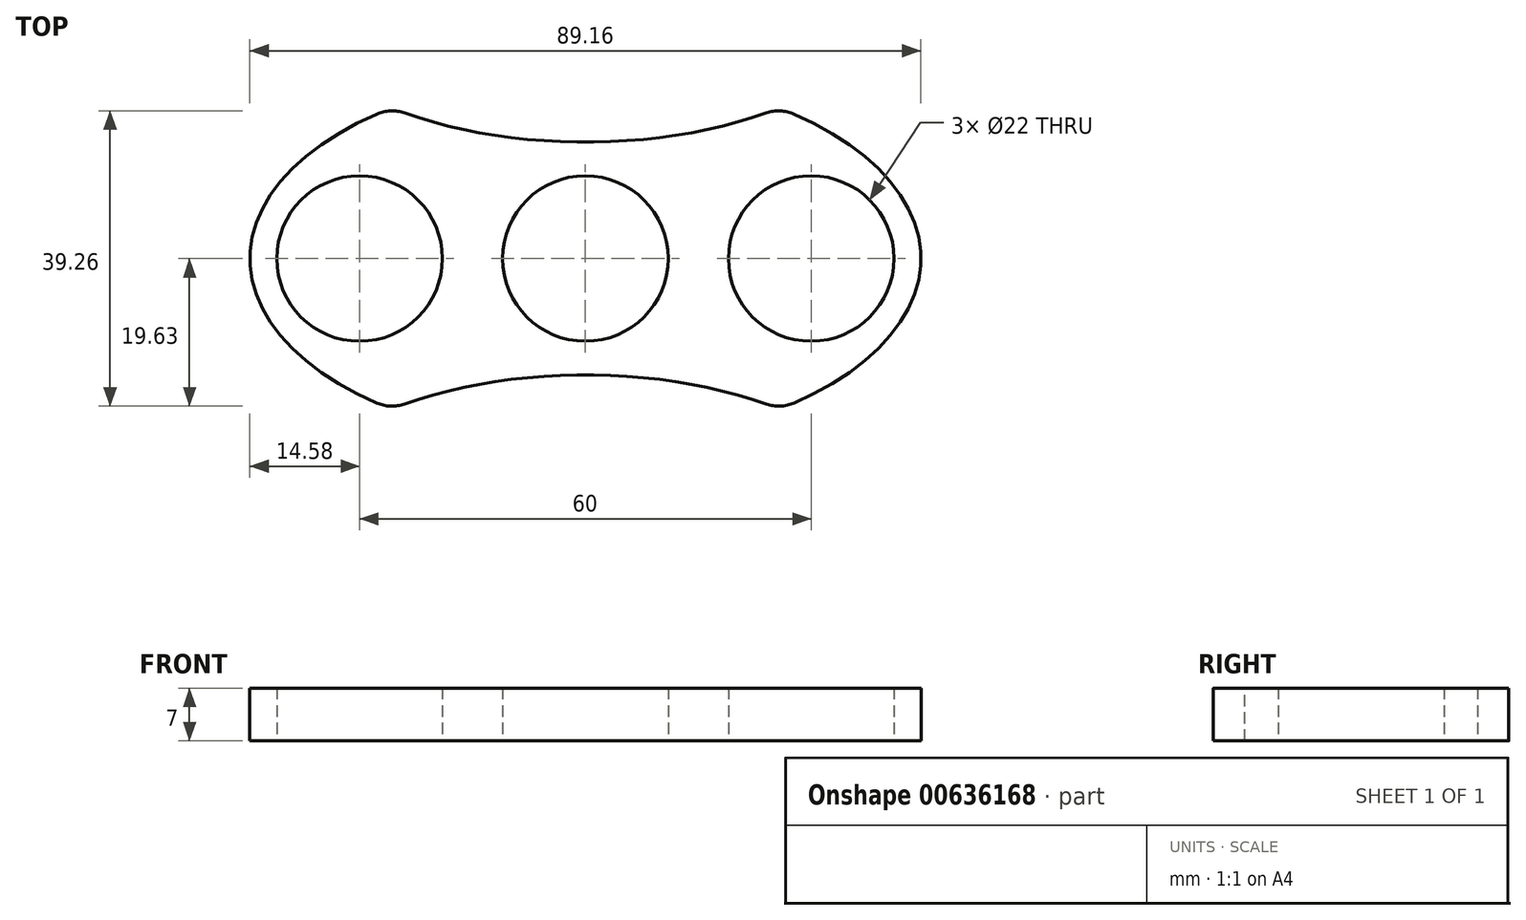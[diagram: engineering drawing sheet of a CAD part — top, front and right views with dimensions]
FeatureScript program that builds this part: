
annotation { "Feature Type Name" : "Feature", "Feature Type Description" : "" }
export const myFeature = defineFeature(function(context is Context, id is Id, definition is map)
    precondition{}
    {
        {
            var Q0;
            Q0=qCreatedBy(makeId("Top.planeOp"),FACE);
            var sketch = newSketch(context, id + "F0", { "sketchPlane" : qUnion([Q0])});
            skCircle(sketch, "E0", {"center": v(0, 0) * mm, "radius": 11 * mm});
            skLineSegment(sketch, "E1", {"start": v(0, 40.08) * mm, "end": v(0, -38.95) * mm, "construction": true});
            skCircle(sketch, "E2", {"center": v(30, 0) * mm, "radius": 11 * mm});
            skCircle(sketch, "E3", {"center": v(-30, 0) * mm, "radius": 11 * mm});
            skEllipse(sketch, "E4", {"center": v(0, 0) * mm, "majorRadius": 44.58 * mm, "minorRadius": 24.53 * mm, "majorAxis": v(1, 0)});
            skEllipticalArc(sketch, "E5.0.1.0", {});
            skLineSegment(sketch, "E5.direction1", {"start": v(0, 0) * mm, "end": v(25, 0) * mm, "construction": true});
            skLineSegment(sketch, "E5.direction2", {"start": v(0, 0) * mm, "end": v(0, 40) * mm, "construction": true});
            skLineSegment(sketch, "E6", {"start": v(-30, 0) * mm, "end": v(30, 0) * mm, "construction": true});
            skEllipticalArc(sketch, "E7.MirrorCS", {});
            const initialGuessF0  = {"E5.0.1.0": [0, 0.04, 1, 0, 0.04458365961909294, 0.024525111976454465, 4.0951691233786285, 5.32960883739075], "E7.MirrorCS": [0, -0.04, 1, 0, 0.04458365961909294, 0.024525111976454465, 0.9535764697888363, 2.1880161838009577]};
            skSetInitialGuess(sketch, initialGuessF0);
            skSolve(sketch);
        }
        {
            var Q0;
            Q0=makeQuery(id+"F0.imprint","IMPRINT",FACE,{"disambiguationData":[TD([[makeQuery(id+"F0.imprint","IMPRINT",EDGE,{"derivedFrom":sQuery(id+"F0.wireOp",EDGE,"E0")}),-1.0]])]});
            extrude(context, id + "F1", {"entities" : qUnion([Q0]), "depth" : 7 * mm, "offsetDistance" : 25 * mm});
        }
        {
            var Q0;
            {var subQ0=sQuery(id+"F0.wireOp",EDGE,"E5.0.1.0");var subQ1=sQuery(id+"F0.wireOp",EDGE,"E4");Q0=makeQuery(id+"F1.opExtrude","SWEPT_EDGE",EDGE,{"disambiguationData":[OSD([subQ1,subQ0]),TDD([makeQuery(id+"F0.imprint","INTERSECT",VERTEX,{"disambiguationData":[OD(0.0)],"derivedFrom":[subQ1,subQ0]})])]});}
            var Q1;
            {var subQ0=sQuery(id+"F0.wireOp",EDGE,"E5.0.1.0");var subQ1=sQuery(id+"F0.wireOp",EDGE,"E4");Q1=makeQuery(id+"F1.opExtrude","SWEPT_EDGE",EDGE,{"disambiguationData":[OSD([subQ1,subQ0]),TDD([makeQuery(id+"F0.imprint","INTERSECT",VERTEX,{"disambiguationData":[OD(1.0)],"derivedFrom":[subQ1,subQ0]})])]});}
            var Q2;
            {var subQ0=sQuery(id+"F0.wireOp",EDGE,"E7.MirrorCS");var subQ1=sQuery(id+"F0.wireOp",EDGE,"E4");Q2=makeQuery(id+"F1.opExtrude","SWEPT_EDGE",EDGE,{"disambiguationData":[OSD([subQ1,subQ0]),TDD([makeQuery(id+"F0.imprint","INTERSECT",VERTEX,{"disambiguationData":[OD(1.0)],"derivedFrom":[subQ1,subQ0]})])]});}
            var Q3;
            {var subQ0=sQuery(id+"F0.wireOp",EDGE,"E7.MirrorCS");var subQ1=sQuery(id+"F0.wireOp",EDGE,"E4");Q3=makeQuery(id+"F1.opExtrude","SWEPT_EDGE",EDGE,{"disambiguationData":[OSD([subQ1,subQ0]),TDD([makeQuery(id+"F0.imprint","INTERSECT",VERTEX,{"disambiguationData":[OD(0.0)],"derivedFrom":[subQ1,subQ0]})])]});}
            fillet(context, id + "F2", {"entities" : qUnion([Q0, Q1, Q2, Q3]), "radius" : 5 * mm, "tangentPropagation" : true, "allowEdgeOverflow" : false});
        }
    });
